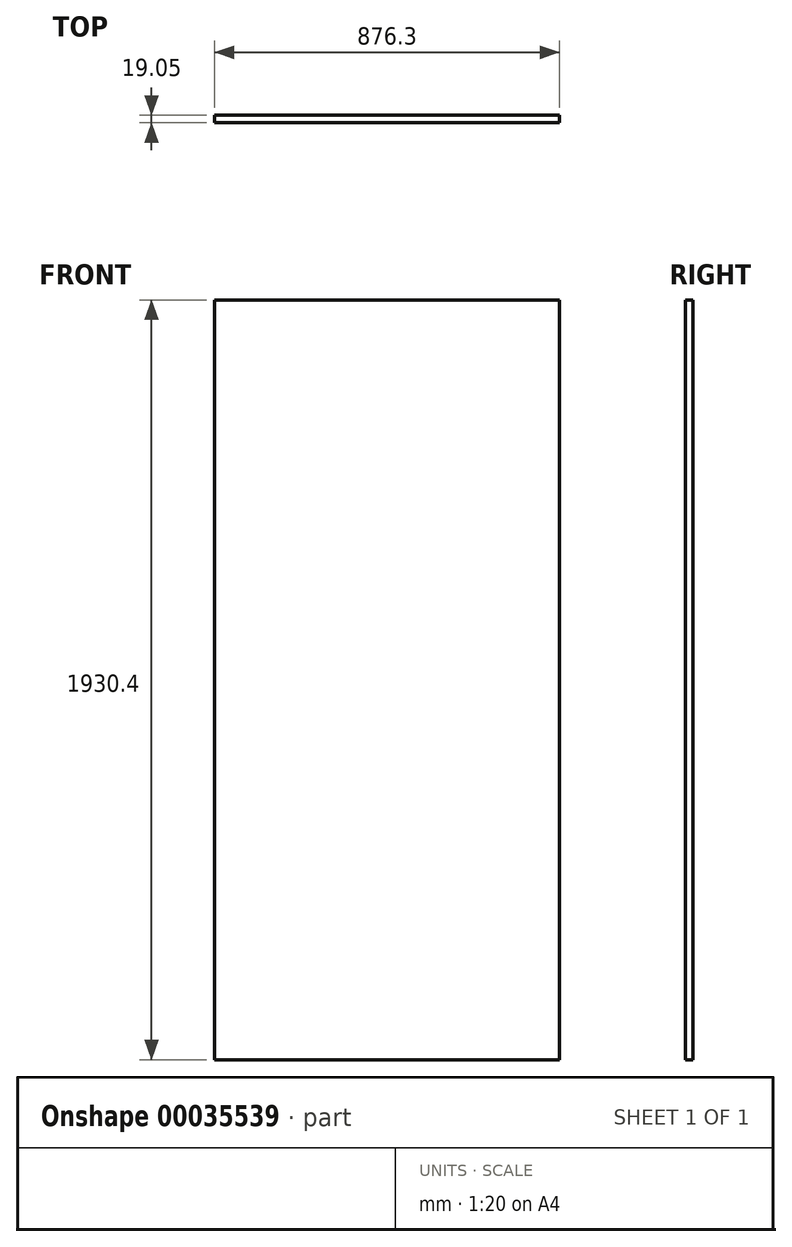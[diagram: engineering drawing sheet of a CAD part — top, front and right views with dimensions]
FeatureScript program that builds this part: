
annotation { "Feature Type Name" : "Feature", "Feature Type Description" : "" }
export const myFeature = defineFeature(function(context is Context, id is Id, definition is map)
    precondition{}
    {
        {
            var Q0;
            Q0=qCreatedBy(makeId("Front.planeOp"),FACE);
            var sketch = newSketch(context, id + "F0", { "sketchPlane" : qUnion([Q0])});
            skLineSegment(sketch, "E0.bottom", {"start": v(-1016.9, 961.68) * mm, "end": v(-140.6, 961.68) * mm});
            skLineSegment(sketch, "E0.top", {"start": v(-1016.9, -968.72) * mm, "end": v(-140.6, -968.72) * mm});
            skLineSegment(sketch, "E0.left", {"start": v(-1016.9, 961.68) * mm, "end": v(-1016.9, -968.72) * mm});
            skLineSegment(sketch, "E0.right", {"start": v(-140.6, 961.68) * mm, "end": v(-140.6, -968.72) * mm});
            skSolve(sketch);
        }
        {
            var Q0;
            Q0=makeQuery(id+"F0.imprint","IMPRINT",FACE,{"disambiguationData":[TD([[makeQuery(id+"F0.imprint","IMPRINT",EDGE,{"derivedFrom":sQuery(id+"F0.wireOp",EDGE,"E0.bottom")}),-1.0]])]});
            extrude(context, id + "F1", {"entities" : qUnion([Q0]), "depth" : 19.05 * mm});
        }
    });
